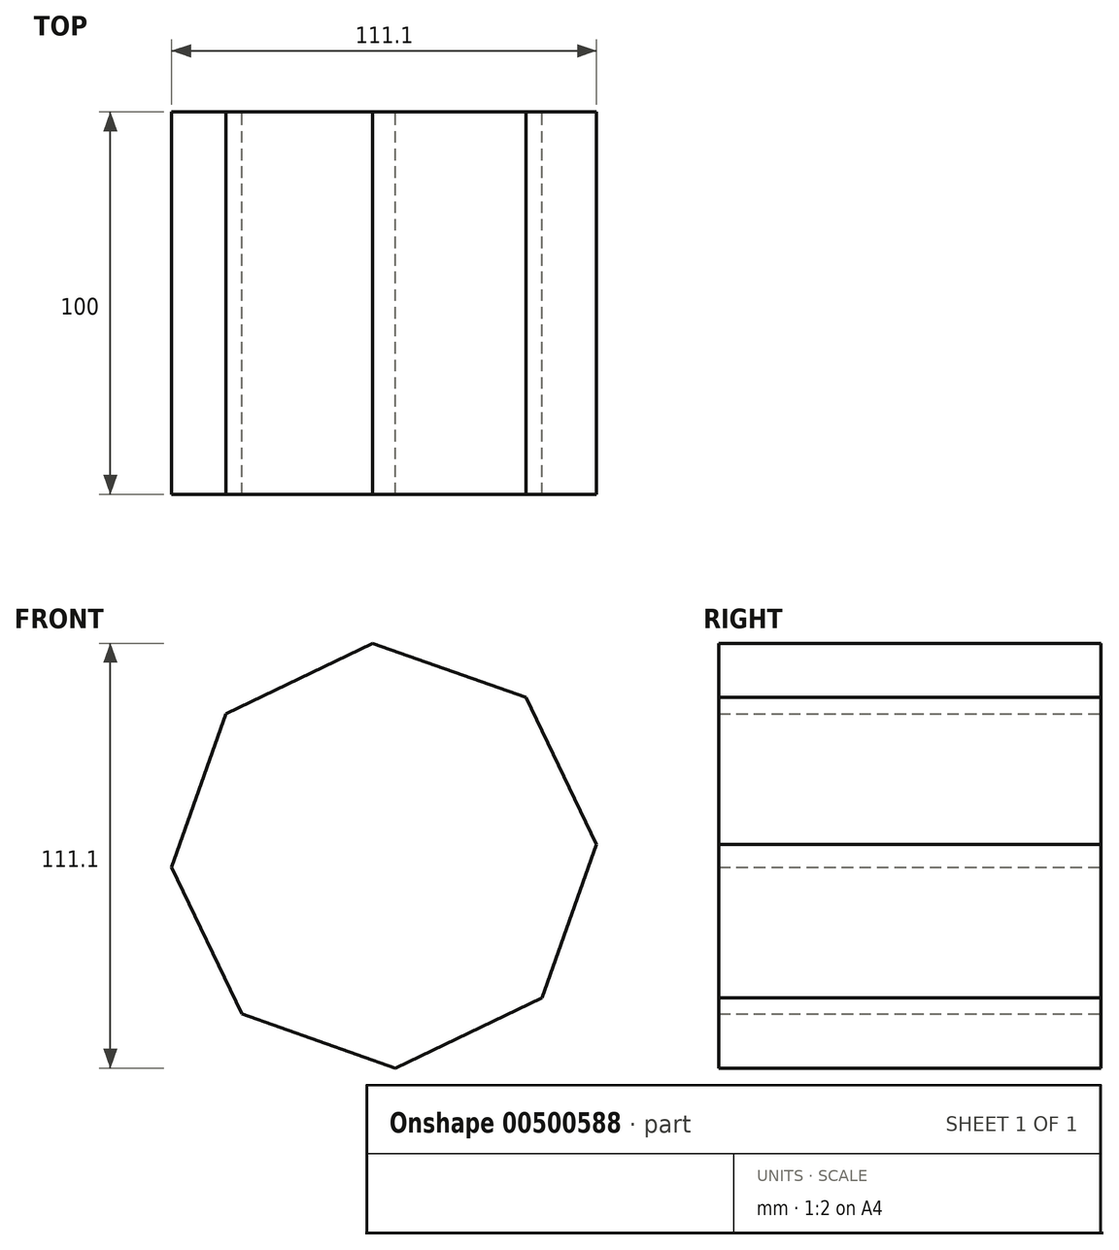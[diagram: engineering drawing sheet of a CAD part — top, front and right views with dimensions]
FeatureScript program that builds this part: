
annotation { "Feature Type Name" : "Feature", "Feature Type Description" : "" }
export const myFeature = defineFeature(function(context is Context, id is Id, definition is map)
    precondition{}
    {
        {
            var Q0;
            Q0=qCreatedBy(makeId("Front.planeOp"),FACE);
            var sketch = newSketch(context, id + "F0", { "sketchPlane" : qUnion([Q0])});
            skCircle(sketch, "E0.cCircle", {"center": v(0, 0) * mm, "radius": 55.63 * mm, "construction": true});
            skLineSegment(sketch, "E0.0", {"start": v(-41.39, 37.16) * mm, "end": v(-2.99, 55.55) * mm});
            skLineSegment(sketch, "E0.1", {"start": v(-2.99, 55.55) * mm, "end": v(37.16, 41.39) * mm});
            skLineSegment(sketch, "E0.2", {"start": v(37.16, 41.39) * mm, "end": v(55.55, 2.99) * mm});
            skLineSegment(sketch, "E0.3", {"start": v(55.55, 2.99) * mm, "end": v(41.39, -37.16) * mm});
            skLineSegment(sketch, "E0.4", {"start": v(41.39, -37.16) * mm, "end": v(2.99, -55.55) * mm});
            skLineSegment(sketch, "E0.5", {"start": v(2.99, -55.55) * mm, "end": v(-37.16, -41.39) * mm});
            skLineSegment(sketch, "E0.6", {"start": v(-37.16, -41.39) * mm, "end": v(-55.55, -2.99) * mm});
            skLineSegment(sketch, "E0.7", {"start": v(-55.55, -2.99) * mm, "end": v(-41.39, 37.16) * mm});
            skSolve(sketch);
        }
        {
            var Q0;
            Q0=makeQuery(id+"F0.imprint","IMPRINT",FACE,{"disambiguationData":[TD([[makeQuery(id+"F0.imprint","IMPRINT",EDGE,{"derivedFrom":sQuery(id+"F0.wireOp",EDGE,"E0.0")}),-1.0]])]});
            extrude(context, id + "F1", {"entities" : qUnion([Q0]), "endBound" : BoundingType.SYMMETRIC, "depth" : 100 * mm});
        }
    });
